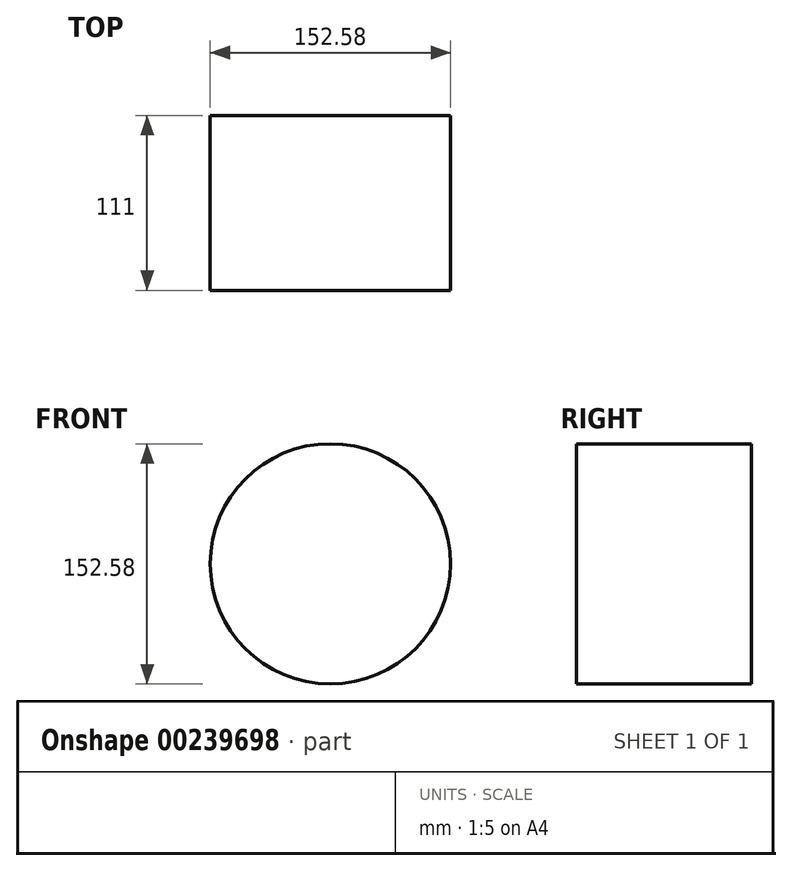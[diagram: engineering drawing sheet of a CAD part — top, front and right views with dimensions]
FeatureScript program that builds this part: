
annotation { "Feature Type Name" : "Feature", "Feature Type Description" : "" }
export const myFeature = defineFeature(function(context is Context, id is Id, definition is map)
    precondition{}
    {
        {
            var Q0;
            Q0=qCreatedBy(makeId("Front.planeOp"),FACE);
            var sketch = newSketch(context, id + "F0", { "sketchPlane" : qUnion([Q0])});
            skCircle(sketch, "E0", {"center": v(0, 0) * mm, "radius": 76.29 * mm});
            skSolve(sketch);
        }
        {
            var Q0;
            Q0 = qSketchRegion(id + "F0", true);
            extrude(context, id + "F1", {"entities" : qUnion([Q0]), "oppositeDirection" : true, "depth" : 111 * mm});
        }
    });
